# Revit family: AIPhone_GT-1M3
name_source: partatom
category: Data Devices
units: mm (PartAtom-declared; Revit-internal decimal feet)

## family parameters
Cut with Voids When Loaded = No
Host = Face
Maintain Annotation Orientation = Yes
OmniClass Number = 23.85.50.17
OmniClass Title = Communication and Data Processing Equipment
Part Type = Normal
Room Calculation Point = No
Round Connector Dimension = Use Diameter
Shared = No

## types (1)
- AIPhone_GT-1M3
    Body = Plastic
    Default Elevation = 48 "
    Depth = 1 "
    Description = RESIDENTIAL / TENANT STATION
    Door Release Button = Door Release
    Green Building-LEED = https://www.arcat.com
    Height = 7.06 "
    Host Width = 12 "
    Installation-Fabrication = https://www.arcat.com
    Manufacturer = AIPHONE
    Manufacturer Fax = 425-455-0071
    Manufacturer Website = www.aiphone.com
    Model = GT-1M3
    Revision = R1.0.0
    Screen = Screen
    Specification = https://www.arcat.com
    Talk Button = Talk Button
    Width = 4.94 "

## geometry (parser evidence)
native form markers: Sweep x2
no freeform markers — native parametric forms only
